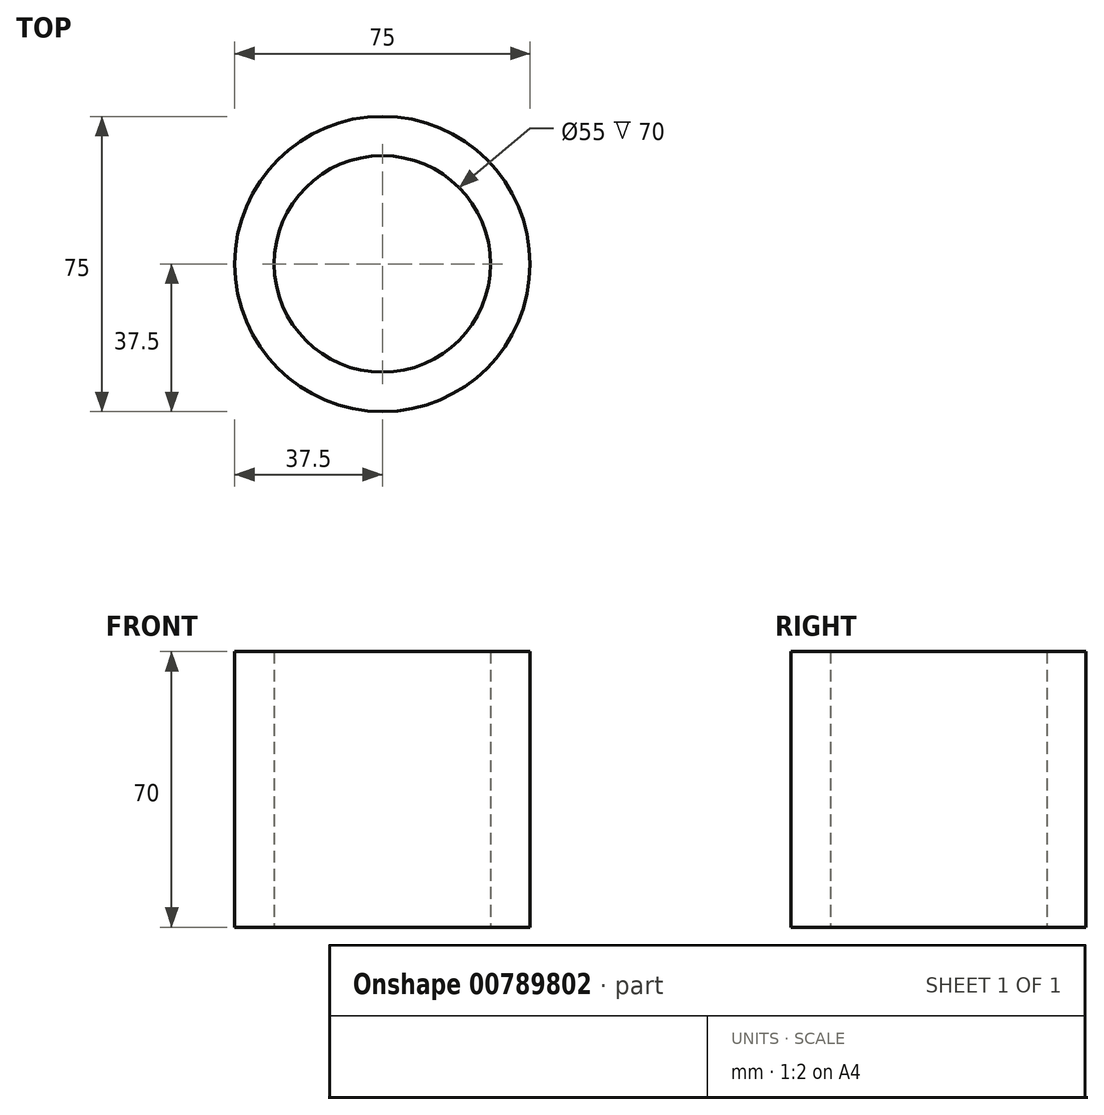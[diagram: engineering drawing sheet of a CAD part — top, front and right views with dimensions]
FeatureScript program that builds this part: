
annotation { "Feature Type Name" : "Feature", "Feature Type Description" : "" }
export const myFeature = defineFeature(function(context is Context, id is Id, definition is map)
    precondition{}
    {
        {
            var Q0;
            Q0=qCreatedBy(makeId("Top.planeOp"),FACE);
            var sketch = newSketch(context, id + "F0", { "sketchPlane" : qUnion([Q0])});
            skCircle(sketch, "E0", {"center": v(0, 0) * mm, "radius": 27.5 * mm});
            skCircle(sketch, "E1", {"center": v(0, 0) * mm, "radius": 37.5 * mm});
            skSolve(sketch);
        }
        {
            var Q0;
            Q0=makeQuery(id+"F0.imprint","IMPRINT",FACE,{"disambiguationData":[TD([[makeQuery(id+"F0.imprint","IMPRINT",EDGE,{"derivedFrom":sQuery(id+"F0.wireOp",EDGE,"E0")}),-1.0]])]});
            extrude(context, id + "F1", {"entities" : qUnion([Q0]), "depth" : 70 * mm, "offsetDistance" : 25 * mm});
        }
    });
